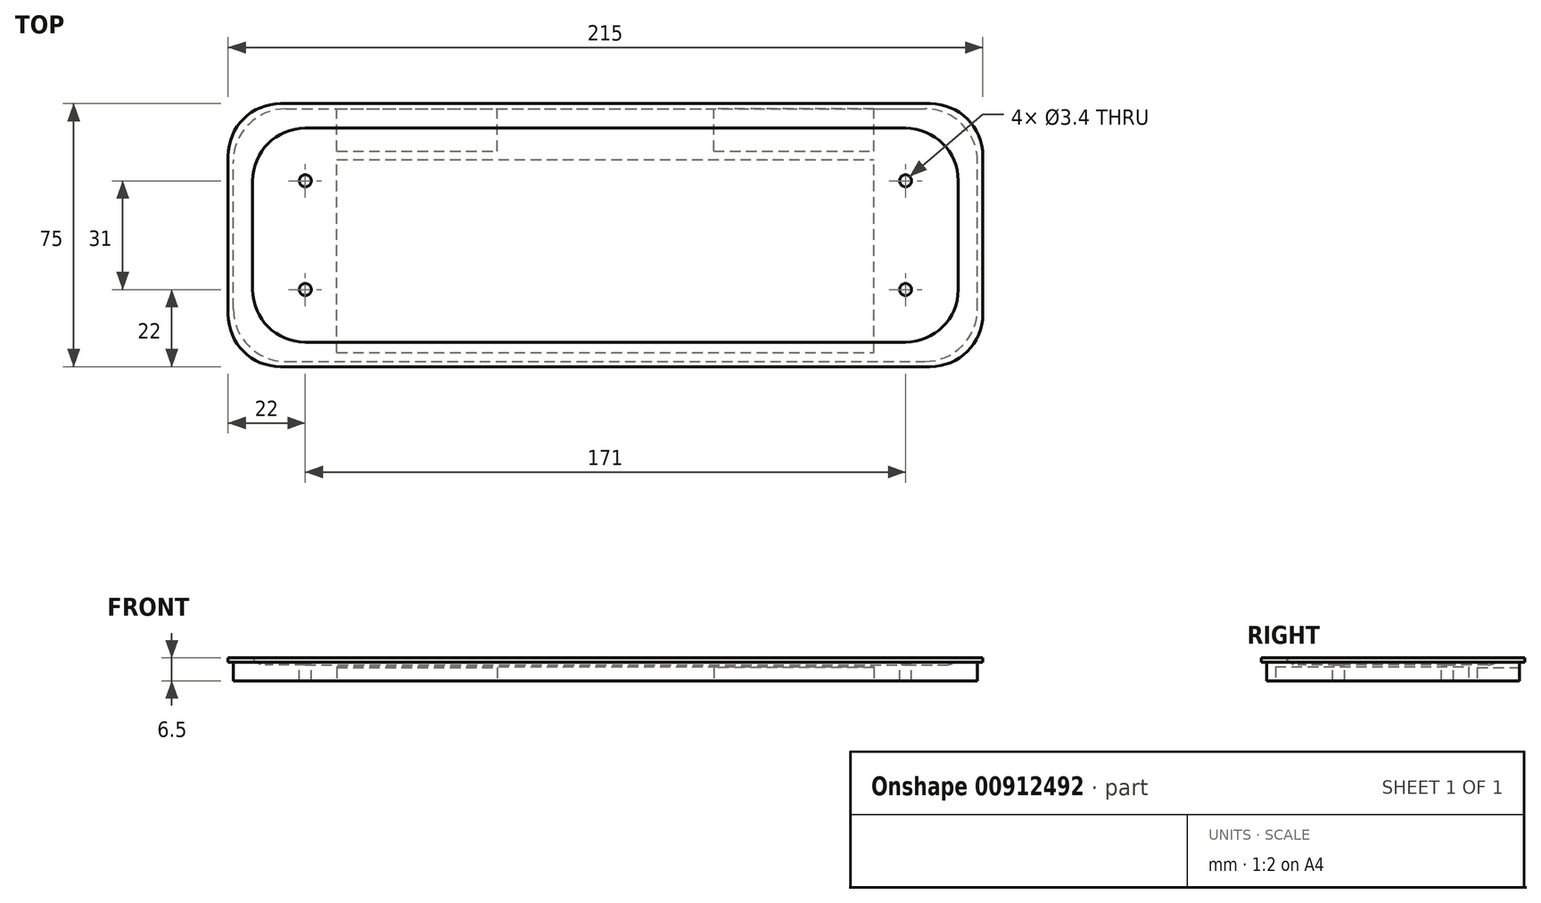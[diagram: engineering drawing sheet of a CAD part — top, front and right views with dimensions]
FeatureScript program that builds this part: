
annotation { "Feature Type Name" : "Feature", "Feature Type Description" : "" }
export const myFeature = defineFeature(function(context is Context, id is Id, definition is map)
    precondition{}
    {
        {
            var Q0;
            Q0=qCreatedBy(makeId("Top.planeOp"),FACE);
            var sketch = newSketch(context, id + "F0", { "sketchPlane" : qUnion([Q0])});
            skLineSegment(sketch, "E0.bottom", {"start": v(-107.5, 37.5) * mm, "end": v(107.5, 37.5) * mm});
            skLineSegment(sketch, "E0.top", {"start": v(-107.5, -37.5) * mm, "end": v(107.5, -37.5) * mm});
            skLineSegment(sketch, "E0.left", {"start": v(-107.5, 37.5) * mm, "end": v(-107.5, -37.5) * mm});
            skLineSegment(sketch, "E0.right", {"start": v(107.5, 37.5) * mm, "end": v(107.5, -37.5) * mm});
            skPoint(sketch, "E0.middle", {"position": v(0, 0) * mm});
            skSolve(sketch);
        }
        {
            var Q0;
            Q0 = qSketchRegion(id + "F0", true);
            extrude(context, id + "F1", {"entities" : qUnion([Q0]), "depth" : 1.25 * mm, "offsetDistance" : 25 * mm});
        }
        {
            var Q0;
            Q0=makeQuery(id+"F1.opExtrude","SWEPT_EDGE",EDGE,{"disambiguationData":[OSD([sQuery(id+"F0.wireOp",EDGE,"E0.top"),sQuery(id+"F0.wireOp",EDGE,"E0.right")])]});
            var Q1;
            Q1=makeQuery(id+"F1.opExtrude","SWEPT_EDGE",EDGE,{"disambiguationData":[OSD([sQuery(id+"F0.wireOp",EDGE,"E0.bottom"),sQuery(id+"F0.wireOp",EDGE,"E0.right")])]});
            var Q2;
            Q2=makeQuery(id+"F1.opExtrude","SWEPT_EDGE",EDGE,{"disambiguationData":[OSD([sQuery(id+"F0.wireOp",EDGE,"E0.bottom"),sQuery(id+"F0.wireOp",EDGE,"E0.left")])]});
            var Q3;
            Q3=makeQuery(id+"F1.opExtrude","SWEPT_EDGE",EDGE,{"disambiguationData":[OSD([sQuery(id+"F0.wireOp",EDGE,"E0.top"),sQuery(id+"F0.wireOp",EDGE,"E0.left")])]});
            fillet(context, id + "F2", {"entities" : qUnion([Q0, Q1, Q2, Q3]), "radius" : 15 * mm, "tangentPropagation" : true, "allowEdgeOverflow" : false});
        }
        {
            var Q0;
            Q0=makeQuery(id+"F1.opExtrude","CAP_FACE",FACE,{"disambiguationData":[OSD([sQuery(id+"F0.wireOp",EDGE,"E0.bottom"),sQuery(id+"F0.wireOp",EDGE,"E0.top"),sQuery(id+"F0.wireOp",EDGE,"E0.left"),sQuery(id+"F0.wireOp",EDGE,"E0.right")])],"isStart":true});
            var sketch = newSketch(context, id + "F3", { "sketchPlane" : qUnion([Q0])});
            skLineSegment(sketch, "E1.bottom", {"start": v(-106, 36) * mm, "end": v(106, 36) * mm});
            skLineSegment(sketch, "E1.top", {"start": v(-106, -36) * mm, "end": v(106, -36) * mm});
            skLineSegment(sketch, "E1.left", {"start": v(-106, 36) * mm, "end": v(-106, -36) * mm});
            skLineSegment(sketch, "E1.right", {"start": v(106, 36) * mm, "end": v(106, -36) * mm});
            skPoint(sketch, "E1.middle", {"position": v(0, 0) * mm});
            skSolve(sketch);
        }
        {
            var Q0;
            Q0 = qSketchRegion(id + "F3", true);
            extrude(context, id + "F4", {"entities" : qUnion([Q0]), "operationType" : NewBodyOperationType.ADD, "depth" : 5.25 * mm, "offsetDistance" : 25 * mm});
        }
        {
            var Q0;
            Q0=makeQuery(id+"F4.opExtrude","SWEPT_EDGE",EDGE,{"disambiguationData":[OSD([sQuery(id+"F3.wireOp",EDGE,"E1.bottom"),sQuery(id+"F3.wireOp",EDGE,"E1.left")])]});
            var Q1;
            Q1=makeQuery(id+"F4.opExtrude","SWEPT_EDGE",EDGE,{"disambiguationData":[OSD([sQuery(id+"F3.wireOp",EDGE,"E1.top"),sQuery(id+"F3.wireOp",EDGE,"E1.left")])]});
            var Q2;
            Q2=makeQuery(id+"F4.opExtrude","SWEPT_EDGE",EDGE,{"disambiguationData":[OSD([sQuery(id+"F3.wireOp",EDGE,"E1.top"),sQuery(id+"F3.wireOp",EDGE,"E1.right")])]});
            var Q3;
            Q3=makeQuery(id+"F4.opExtrude","SWEPT_EDGE",EDGE,{"disambiguationData":[OSD([sQuery(id+"F3.wireOp",EDGE,"E1.bottom"),sQuery(id+"F3.wireOp",EDGE,"E1.right")])]});
            fillet(context, id + "F5", {"entities" : qUnion([Q0, Q1, Q2, Q3]), "radius" : 15 * mm, "tangentPropagation" : true, "allowEdgeOverflow" : false});
        }
        {
            var Q0;
            Q0=makeQuery(id+"F1.opExtrude","CAP_FACE",FACE,{"disambiguationData":[OSD([sQuery(id+"F0.wireOp",EDGE,"E0.bottom"),sQuery(id+"F0.wireOp",EDGE,"E0.top"),sQuery(id+"F0.wireOp",EDGE,"E0.left"),sQuery(id+"F0.wireOp",EDGE,"E0.right")])],"isStart":false});
            var sketch = newSketch(context, id + "F6", { "sketchPlane" : qUnion([Q0])});
            skLineSegment(sketch, "E2.bottom", {"start": v(-106, 36) * mm, "end": v(106, 36) * mm});
            skLineSegment(sketch, "E2.top", {"start": v(-106, -36) * mm, "end": v(106, -36) * mm});
            skLineSegment(sketch, "E2.left", {"start": v(-106, 36) * mm, "end": v(-106, -36) * mm});
            skLineSegment(sketch, "E2.right", {"start": v(106, 36) * mm, "end": v(106, -36) * mm});
            skPoint(sketch, "E2.middle", {"position": v(0, 0) * mm});
            skSolve(sketch);
        }
        {
            var Q0;
            Q0=makeQuery(id+"F6.imprint","IMPRINT",FACE,{"disambiguationData":[TD([[makeQuery(id+"F6.imprint","IMPRINT",EDGE,{"derivedFrom":sQuery(id+"F6.wireOp",EDGE,"E2.bottom")}),-1.0]])]});
            var sketch = newSketch(context, id + "F7", { "sketchPlane" : qUnion([Q0])});
            skLineSegment(sketch, "E3.bottom", {"start": v(-100.5, 30.5) * mm, "end": v(100.5, 30.5) * mm});
            skLineSegment(sketch, "E3.top", {"start": v(-100.5, -30.5) * mm, "end": v(100.5, -30.5) * mm});
            skLineSegment(sketch, "E3.left", {"start": v(-100.5, 30.5) * mm, "end": v(-100.5, -30.5) * mm});
            skLineSegment(sketch, "E3.right", {"start": v(100.5, 30.5) * mm, "end": v(100.5, -30.5) * mm});
            skPoint(sketch, "E3.middle", {"position": v(0, 0) * mm});
            skSolve(sketch);
        }
        {
            var Q0;
            Q0 = qSketchRegion(id + "F7", true);
            extrude(context, id + "F8", {"entities" : qUnion([Q0]), "operationType" : NewBodyOperationType.REMOVE, "oppositeDirection" : true, "depth" : 2 * mm, "offsetDistance" : 25 * mm});
        }
        {
            var Q0;
            Q0=makeQuery(id+"F8.boolean.opBoolean","COPY",EDGE,{"derivedFrom":makeQuery(id+"F8.opExtrude","SWEPT_EDGE",EDGE,{"disambiguationData":[OSD([sQuery(id+"F7.wireOp",EDGE,"E3.bottom"),sQuery(id+"F7.wireOp",EDGE,"E3.left")])]})});
            var Q1;
            Q1=makeQuery(id+"F8.boolean.opBoolean","COPY",EDGE,{"derivedFrom":makeQuery(id+"F8.opExtrude","SWEPT_EDGE",EDGE,{"disambiguationData":[OSD([sQuery(id+"F7.wireOp",EDGE,"E3.top"),sQuery(id+"F7.wireOp",EDGE,"E3.left")])]})});
            var Q2;
            Q2=makeQuery(id+"F8.boolean.opBoolean","COPY",EDGE,{"derivedFrom":makeQuery(id+"F8.opExtrude","SWEPT_EDGE",EDGE,{"disambiguationData":[OSD([sQuery(id+"F7.wireOp",EDGE,"E3.bottom"),sQuery(id+"F7.wireOp",EDGE,"E3.right")])]})});
            var Q3;
            Q3=makeQuery(id+"F8.boolean.opBoolean","COPY",EDGE,{"derivedFrom":makeQuery(id+"F8.opExtrude","SWEPT_EDGE",EDGE,{"disambiguationData":[OSD([sQuery(id+"F7.wireOp",EDGE,"E3.top"),sQuery(id+"F7.wireOp",EDGE,"E3.right")])]})});
            fillet(context, id + "F9", {"entities" : qUnion([Q0, Q1, Q2, Q3]), "radius" : 15 * mm, "tangentPropagation" : true, "allowEdgeOverflow" : false});
        }
        {
            var Q0;
            Q0=makeQuery(id+"F8.boolean.opBoolean","COPY",EDGE,{"derivedFrom":makeQuery(id+"F8.opExtrude","CAP_EDGE",EDGE,{"disambiguationData":[OSD([sQuery(id+"F7.wireOp",EDGE,"E3.left")])],"isStart":false})});
            fillet(context, id + "F10", {"entities" : qUnion([Q0]), "radius" : 4 * mm, "tangentPropagation" : true, "allowEdgeOverflow" : false});
        }
        {
            var Q0;
            Q0=makeQuery(id+"F4.opExtrude","SWEPT_FACE",FACE,{"disambiguationData":[OSD([sQuery(id+"F3.wireOp",EDGE,"E1.top")])]});
            var sketch = newSketch(context, id + "F11", { "sketchPlane" : qUnion([Q0])});
            skLineSegment(sketch, "E4.bottom", {"start": v(-76.5, -1.5) * mm, "end": v(-30.88, -1.5) * mm});
            skLineSegment(sketch, "E4.top", {"start": v(-76.5, -5.25) * mm, "end": v(-30.88, -5.25) * mm});
            skLineSegment(sketch, "E4.left", {"start": v(-76.5, -1.5) * mm, "end": v(-76.5, -5.25) * mm});
            skLineSegment(sketch, "E4.right", {"start": v(-30.88, -1.5) * mm, "end": v(-30.88, -5.25) * mm});
            skLineSegment(sketch, "E5.bottom", {"start": v(76.5, -1.5) * mm, "end": v(30.88, -1.5) * mm});
            skLineSegment(sketch, "E5.top", {"start": v(76.5, -5.25) * mm, "end": v(30.88, -5.25) * mm});
            skLineSegment(sketch, "E5.left", {"start": v(76.5, -1.5) * mm, "end": v(76.5, -5.25) * mm});
            skLineSegment(sketch, "E5.right", {"start": v(30.88, -1.5) * mm, "end": v(30.88, -5.25) * mm});
            skSolve(sketch);
        }
        {
            var Q0;
            Q0 = qSketchRegion(id + "F11", true);
            extrude(context, id + "F12", {"entities" : qUnion([Q0]), "operationType" : NewBodyOperationType.REMOVE, "oppositeDirection" : true, "depth" : 12 * mm, "offsetDistance" : 25 * mm});
        }
        {
            var Q0;
            Q0=makeQuery(id+"F4.opExtrude","CAP_FACE",FACE,{"disambiguationData":[OSD([sQuery(id+"F3.wireOp",EDGE,"E1.bottom"),sQuery(id+"F3.wireOp",EDGE,"E1.top"),sQuery(id+"F3.wireOp",EDGE,"E1.left"),sQuery(id+"F3.wireOp",EDGE,"E1.right")])],"isStart":false});
            var sketch = newSketch(context, id + "F13", { "sketchPlane" : qUnion([Q0])});
            skLineSegment(sketch, "E6.bottom", {"start": v(-76.5, 33.5) * mm, "end": v(76.5, 33.5) * mm});
            skLineSegment(sketch, "E6.top", {"start": v(-76.5, -21.5) * mm, "end": v(76.5, -21.5) * mm});
            skLineSegment(sketch, "E6.left", {"start": v(-76.5, 33.5) * mm, "end": v(-76.5, -21.5) * mm});
            skLineSegment(sketch, "E6.right", {"start": v(76.5, 33.5) * mm, "end": v(76.5, -21.5) * mm});
            skPoint(sketch, "E6.middle", {"position": v(0, 0) * mm});
            skSolve(sketch);
        }
        {
            var Q0;
            Q0 = qSketchRegion(id + "F13", true);
            extrude(context, id + "F14", {"entities" : qUnion([Q0]), "operationType" : NewBodyOperationType.REMOVE, "oppositeDirection" : true, "depth" : 4 * mm, "offsetDistance" : 25 * mm});
        }
        {
            var Q0;
            {var subQ1=sQuery(id+"F0.wireOp",EDGE,"E0.right");var subQ2=sQuery(id+"F0.wireOp",EDGE,"E0.left");var subQ3=sQuery(id+"F0.wireOp",EDGE,"E0.top");var subQ4=sQuery(id+"F0.wireOp",EDGE,"E0.bottom");var subQ5=makeQuery(id+"F1.opExtrude","CAP_FACE",FACE,{"disambiguationData":[OSD([subQ4,subQ3,subQ2,subQ1])],"isStart":false});var subQ10=sQuery(id+"F6.wireOp",EDGE,"E2.bottom");var subQ13=makeQuery(id+"F2.opFillet","BLEND_EDGE",EDGE,{"blendedFrom":[makeQuery(id+"F1.opExtrude","SWEPT_EDGE",EDGE,{"disambiguationData":[OSD([subQ4,subQ2])]}),subQ5],"blendedInto":[subQ5]});var subQ17=makeQuery(id+"F6.imprint","INTERSECT",VERTEX,{"derivedFrom":[subQ13,subQ10]});Q0=makeQuery(id+"F6.imprint","IMPRINT",FACE,{"disambiguationData":[TD([[makeQuery(id+"F6.imprint","IMPRINT",EDGE,{"disambiguationData":[TD([[subQ17,-1.0]])],"derivedFrom":subQ10}),-1.0]])]});}
            var sketch = newSketch(context, id + "F15", { "sketchPlane" : qUnion([Q0])});
            skPoint(sketch, "E7", {"position": v(-85.5, 15.5) * mm});
            skPoint(sketch, "E8", {"position": v(-85.5, -15.5) * mm});
            skPoint(sketch, "E9", {"position": v(85.5, 15.5) * mm});
            skPoint(sketch, "E10", {"position": v(85.5, -15.5) * mm});
            skSolve(sketch);
        }
        {
            var Q0;
            Q0=sQuery(id+"F15.wireOp",VERTEX,"E7");
            var Q1;
            Q1=sQuery(id+"F15.wireOp",VERTEX,"E8");
            var Q2;
            Q2=sQuery(id+"F15.wireOp",VERTEX,"E9");
            var Q3;
            Q3=sQuery(id+"F15.wireOp",VERTEX,"E10");
            var Q4;
            Q4=makeQuery(id+"F1.opExtrude","SWEPT_BODY",BODY,{"disambiguationData":[OSD([sQuery(id+"F0.wireOp",EDGE,"E0.bottom"),sQuery(id+"F0.wireOp",EDGE,"E0.top"),sQuery(id+"F0.wireOp",EDGE,"E0.left"),sQuery(id+"F0.wireOp",EDGE,"E0.right")])]});
            hole(context, id + "F16", {"style" : HoleStyle.SIMPLE, "endStyle" : HoleEndStyle.THROUGH, "standardTappedOrClearance" : lookupTablePath({ "fit" : "Normal", "standard" : "ISO", "size" : "M3", "type" : "Clearance" }), "standardBlindInLast" : lookupTablePath({ "fit" : "Normal", "standard" : "ISO", "size" : "M3", "type" : "Clearance" }), "holeDiameter" : 3.4 * mm, "majorDiameter" : 5 * mm, "isTappedThrough" : true, "tappedDepth" : 12 * mm, "tapClearance" : 3, "locations" : qUnion([Q0, Q1, Q2, Q3]), "scope" : qUnion([Q4])});
        }
    });
